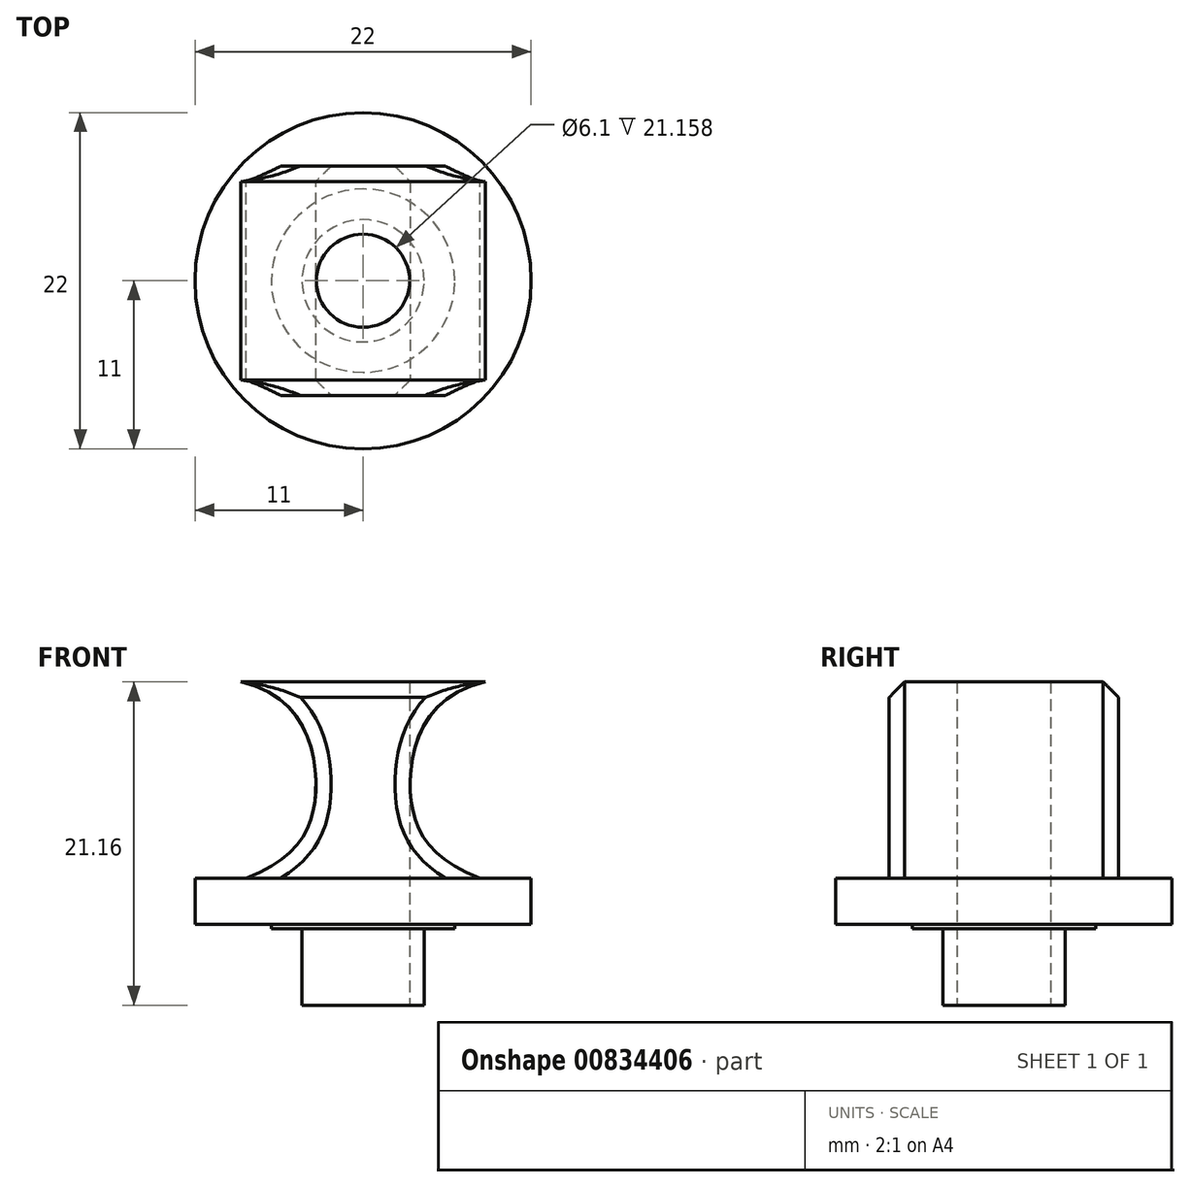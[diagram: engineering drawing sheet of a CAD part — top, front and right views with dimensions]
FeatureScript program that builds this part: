
annotation { "Feature Type Name" : "Feature", "Feature Type Description" : "" }
export const myFeature = defineFeature(function(context is Context, id is Id, definition is map)
    precondition{}
    {
        {
            var Q0;
            Q0=qCreatedBy(makeId("Top.planeOp"),FACE);
            var sketch = newSketch(context, id + "F0", { "sketchPlane" : qUnion([Q0])});
            skCircle(sketch, "E0", {"center": v(0, 0) * mm, "radius": 4 * mm});
            skCircle(sketch, "E1", {"center": v(0, 0) * mm, "radius": 11 * mm});
            skCircle(sketch, "E2", {"center": v(0, 0) * mm, "radius": 3.05 * mm});
            skCircle(sketch, "E3", {"center": v(0, 0) * mm, "radius": 6 * mm});
            skSolve(sketch);
        }
        {
            var Q0;
            Q0=makeQuery(id+"F0.imprint","IMPRINT",FACE,{"disambiguationData":[TD([[makeQuery(id+"F0.imprint","IMPRINT",EDGE,{"derivedFrom":sQuery(id+"F0.wireOp",EDGE,"E0")}),-1.0]])]});
            var Q1;
            Q1=makeQuery(id+"F0.imprint","IMPRINT",FACE,{"disambiguationData":[TD([[makeQuery(id+"F0.imprint","IMPRINT",EDGE,{"derivedFrom":sQuery(id+"F0.wireOp",EDGE,"jqpkiQzC-mYEm-Jatf-0uhs-0JewHfNxIGlt")}),-1.0]])]});
            var Q2;
            Q2=makeQuery(id+"F0.imprint","IMPRINT",FACE,{"disambiguationData":[TD([[makeQuery(id+"F0.imprint","IMPRINT",EDGE,{"derivedFrom":sQuery(id+"F0.wireOp",EDGE,"E1")}),1.0]])]});
            var Q3;
            Q3=makeQuery(id+"F0.imprint","IMPRINT",FACE,{"disambiguationData":[TD([[makeQuery(id+"F0.imprint","IMPRINT",EDGE,{"derivedFrom":sQuery(id+"F0.wireOp",EDGE,"E0")}),1.0]])]});
            var Q4;
            Q4=makeQuery(id+"F0.imprint","IMPRINT",FACE,{"disambiguationData":[TD([[makeQuery(id+"F0.imprint","IMPRINT",EDGE,{"derivedFrom":sQuery(id+"F0.wireOp",EDGE,"E2")}),1.0]])]});
            extrude(context, id + "F1", {"entities" : qUnion([Q0, Q1, Q2, Q3, Q4]), "depth" : 3 * mm, "offsetDistance" : 25 * mm});
        }
        {
            var Q0;
            Q0=qCreatedBy(makeId("Front.planeOp"),FACE);
            var sketch = newSketch(context, id + "F2", { "sketchPlane" : qUnion([Q0])});
            skLineSegment(sketch, "E4", {"start": v(0, 15.86) * mm, "end": v(-8, 15.86) * mm});
            skFitSpline(sketch, "E5", {"points": [v(-8, 15.86) * mm, v(-3.1, 8.64) * mm, v(-8, 2.86) * mm], "startDerivative": vector(23.95, -5.22) * mm, "endDerivative": vector(-23, -8.74) * mm});
            skLineSegment(sketch, "E6", {"start": v(-8, 2.86) * mm, "end": v(0, 2.86) * mm});
            skLineSegment(sketch, "E7.MirrorCS", {"start": v(0, 15.86) * mm, "end": v(8, 15.86) * mm});
            skFitSpline(sketch, "E8.MirrorCS", {"points": [v(8, 15.86) * mm, v(3.1, 8.64) * mm, v(8, 2.86) * mm], "startDerivative": vector(-23.95, -5.22) * mm, "endDerivative": vector(23, -8.74) * mm});
            skLineSegment(sketch, "E9.MirrorCS", {"start": v(8, 2.86) * mm, "end": v(0, 2.86) * mm});
            skSolve(sketch);
        }
        {
            var Q0;
            Q0=makeQuery(id+"F2.imprint","IMPRINT",FACE,{"disambiguationData":[TD([[makeQuery(id+"F2.imprint","IMPRINT",EDGE,{"derivedFrom":sQuery(id+"F2.wireOp",EDGE,"E4")}),1.0]])]});
            extrude(context, id + "F3", {"entities" : qUnion([Q0]), "operationType" : NewBodyOperationType.ADD, "endBound" : BoundingType.SYMMETRIC, "depth" : 15 * mm, "offsetDistance" : 25 * mm});
        }
        {
            var Q0;
            Q0=makeQuery(id+"F0.imprint","IMPRINT",FACE,{"disambiguationData":[TD([[makeQuery(id+"F0.imprint","IMPRINT",EDGE,{"derivedFrom":sQuery(id+"F0.wireOp",EDGE,"E2")}),1.0]])]});
            extrude(context, id + "F4", {"entities" : qUnion([Q0]), "operationType" : NewBodyOperationType.REMOVE, "depth" : 25 * mm, "offsetDistance" : 25 * mm});
        }
        {
            var Q0;
            Q0=makeQuery(id+"F3.opExtrude","CAP_EDGE",EDGE,{"disambiguationData":[OSD([sQuery(id+"F2.wireOp",EDGE,"E5")])],"isStart":false});
            var Q1;
            Q1=makeQuery(id+"F3.opExtrude","CAP_EDGE",EDGE,{"disambiguationData":[OSD([sQuery(id+"F2.wireOp",EDGE,"E8.MirrorCS")])],"isStart":false});
            var Q2;
            Q2=makeQuery(id+"F3.opExtrude","CAP_EDGE",EDGE,{"disambiguationData":[OSD([sQuery(id+"F2.wireOp",EDGE,"E8.MirrorCS")])],"isStart":true});
            var Q3;
            Q3=makeQuery(id+"F3.opExtrude","CAP_EDGE",EDGE,{"disambiguationData":[OSD([sQuery(id+"F2.wireOp",EDGE,"E5")])],"isStart":true});
            var Q4;
            Q4=makeQuery(id+"F3.opExtrude","CAP_EDGE",EDGE,{"disambiguationData":[OSD([sQuery(id+"F2.wireOp",EDGE,"E4"),sQuery(id+"F2.wireOp",EDGE,"E7.MirrorCS")])],"isStart":true});
            var Q5;
            Q5=makeQuery(id+"F3.opExtrude","CAP_EDGE",EDGE,{"disambiguationData":[OSD([sQuery(id+"F2.wireOp",EDGE,"E4"),sQuery(id+"F2.wireOp",EDGE,"E7.MirrorCS")])],"isStart":false});
            chamfer(context, id + "F5", {"entities" : qUnion([Q0, Q1, Q2, Q3, Q4, Q5]), "width" : 1 * mm, "tangentPropagation" : true});
        }
        {
            var Q0;
            Q0=makeQuery(id+"F0.imprint","IMPRINT",FACE,{"disambiguationData":[TD([[makeQuery(id+"F0.imprint","IMPRINT",EDGE,{"derivedFrom":sQuery(id+"F0.wireOp",EDGE,"E3")}),1.0]])]});
            var Q1;
            {var subQ0=sQuery(id+"F0.wireOp",EDGE,"JMGGA5fA-osfe-nm3D-rLQ8-lUBWGmXbawQh");var subQ1=sQuery(id+"F0.wireOp",EDGE,"E0");var subQ2=makeQuery(id+"F0.imprint","INTERSECT",VERTEX,{"derivedFrom":[subQ1,subQ0]});Q1=makeQuery(id+"F0.imprint","IMPRINT",FACE,{"disambiguationData":[TD([[makeQuery(id+"F0.imprint","IMPRINT",EDGE,{"disambiguationData":[TD([[subQ2,-1.0]])],"derivedFrom":subQ1}),1.0]])]});}
            extrude(context, id + "F6", {"entities" : qUnion([Q0, Q1]), "operationType" : NewBodyOperationType.ADD, "oppositeDirection" : true, "depth" : .3 * mm, "offsetDistance" : 25 * mm});
        }
        {
            var Q0;
            {var subQ0=sQuery(id+"F0.wireOp",EDGE,"JMGGA5fA-osfe-nm3D-rLQ8-lUBWGmXbawQh");var subQ1=sQuery(id+"F0.wireOp",EDGE,"E0");var subQ2=makeQuery(id+"F0.imprint","INTERSECT",VERTEX,{"derivedFrom":[subQ1,subQ0]});Q0=makeQuery(id+"F0.imprint","IMPRINT",FACE,{"disambiguationData":[TD([[makeQuery(id+"F0.imprint","IMPRINT",EDGE,{"disambiguationData":[TD([[subQ2,1.0]])],"derivedFrom":subQ1}),1.0]])]});}
            var Q1;
            {var subQ0=sQuery(id+"F0.wireOp",EDGE,"JMGGA5fA-osfe-nm3D-rLQ8-lUBWGmXbawQh");var subQ1=sQuery(id+"F0.wireOp",EDGE,"E0");var subQ2=makeQuery(id+"F0.imprint","INTERSECT",VERTEX,{"derivedFrom":[subQ1,subQ0]});Q1=makeQuery(id+"F0.imprint","IMPRINT",FACE,{"disambiguationData":[TD([[makeQuery(id+"F0.imprint","IMPRINT",EDGE,{"disambiguationData":[TD([[subQ2,-1.0]])],"derivedFrom":subQ1}),1.0]])]});}
            extrude(context, id + "F7", {"entities" : qUnion([Q0, Q1]), "operationType" : NewBodyOperationType.ADD, "oppositeDirection" : true, "depth" : 5.3 * mm, "offsetDistance" : 25 * mm});
        }
    });
